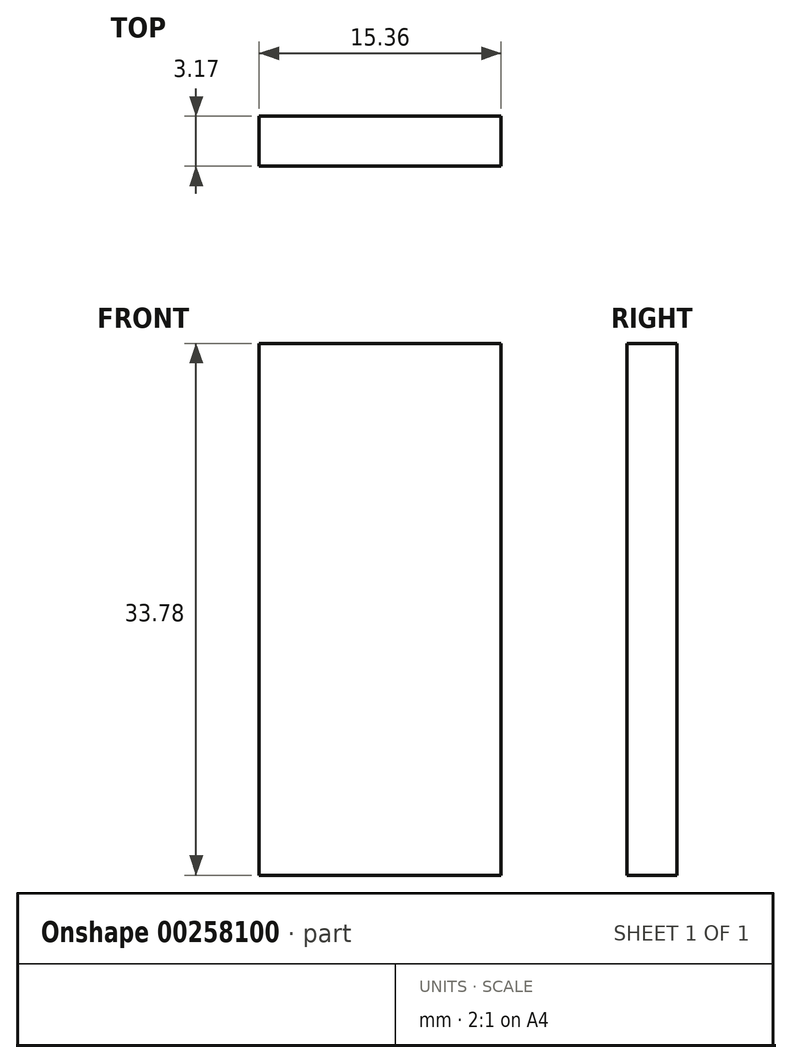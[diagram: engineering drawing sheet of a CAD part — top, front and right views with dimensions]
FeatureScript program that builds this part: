
annotation { "Feature Type Name" : "Feature", "Feature Type Description" : "" }
export const myFeature = defineFeature(function(context is Context, id is Id, definition is map)
    precondition{}
    {
        {
            var Q0;
            Q0=qCreatedBy(makeId("Front.planeOp"),FACE);
            var sketch = newSketch(context, id + "F0", { "sketchPlane" : qUnion([Q0])});
            skLineSegment(sketch, "E0.bottom", {"start": v(-7.68, -16.9) * mm, "end": v(7.68, -16.9) * mm});
            skLineSegment(sketch, "E0.top", {"start": v(-7.68, 16.9) * mm, "end": v(7.68, 16.9) * mm});
            skLineSegment(sketch, "E0.left", {"start": v(-7.68, -16.9) * mm, "end": v(-7.68, 16.9) * mm});
            skLineSegment(sketch, "E0.right", {"start": v(7.68, -16.9) * mm, "end": v(7.68, 16.9) * mm});
            skPoint(sketch, "E0.middle", {"position": v(0, 0) * mm});
            skSolve(sketch);
        }
        {
            var Q0;
            Q0=makeQuery(id+"F0.imprint","IMPRINT",FACE,{"disambiguationData":[TD([[makeQuery(id+"F0.imprint","IMPRINT",EDGE,{"derivedFrom":sQuery(id+"F0.wireOp",EDGE,"E0.bottom")}),1.0]])]});
            extrude(context, id + "F1", {"entities" : qUnion([Q0]), "depth" : 3.17 * mm});
        }
    });
